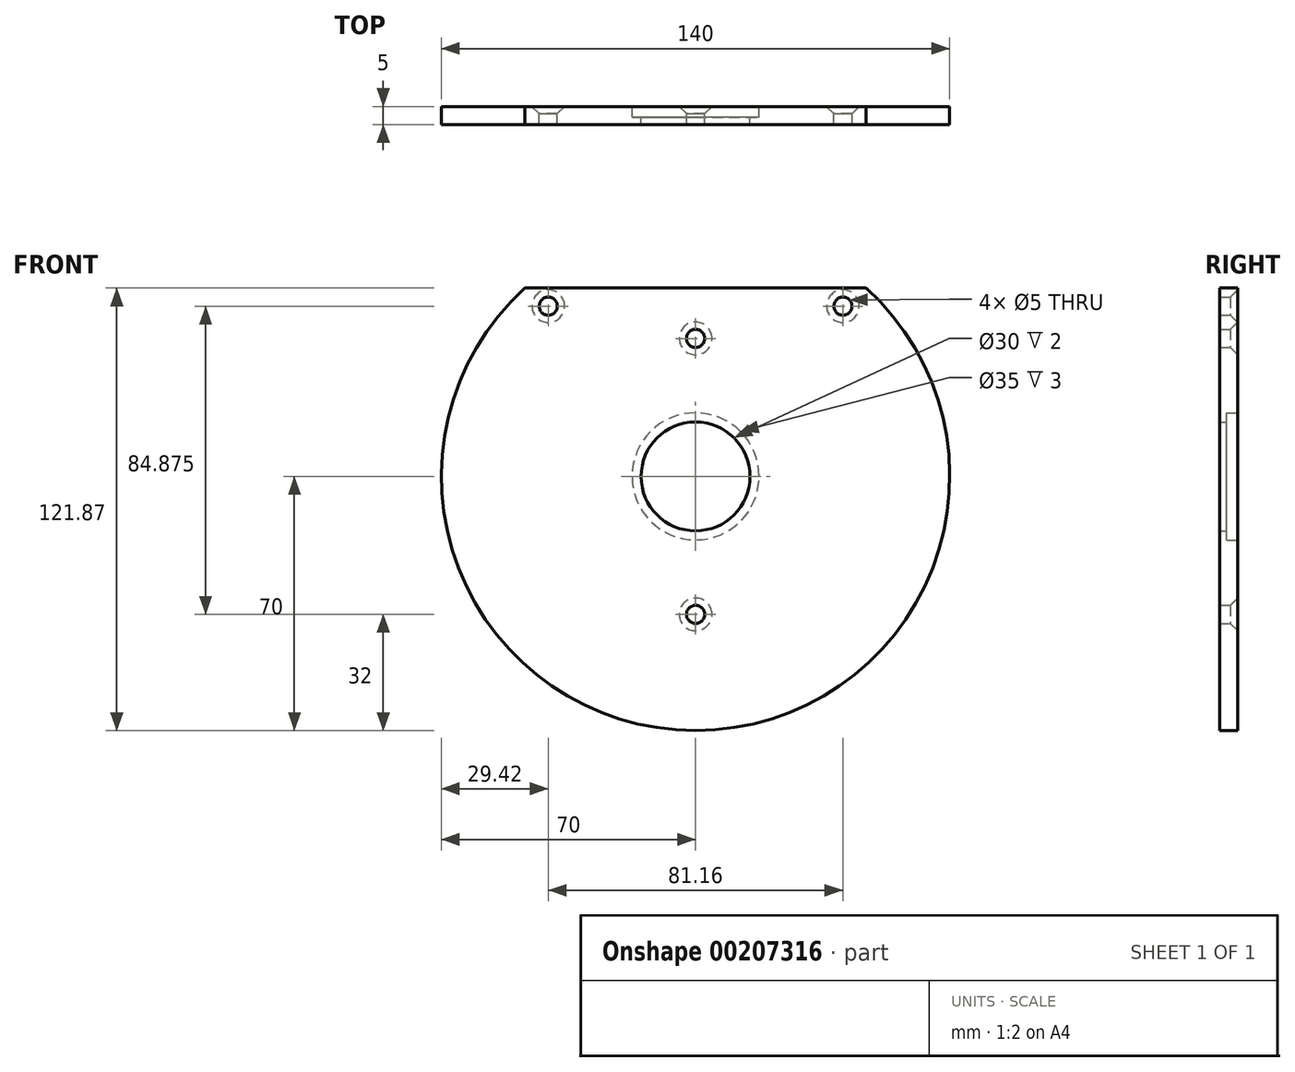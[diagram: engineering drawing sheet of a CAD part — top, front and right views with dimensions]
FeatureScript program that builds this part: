
annotation { "Feature Type Name" : "Feature", "Feature Type Description" : "" }
export const myFeature = defineFeature(function(context is Context, id is Id, definition is map)
    precondition{}
    {
        {
            assignVariable(context, id + "F0", {"name" : "T", "anyValue" : 5});
        }
        {
            assignVariable(context, id + "F1", {"name" : "dia", "anyValue" : 5});
        }
        {
            var Q0;
            Q0=qCreatedBy(makeId("Front.planeOp"),FACE);
            var sketch = newSketch(context, id + "F2", { "sketchPlane" : qUnion([Q0])});
            skArc(sketch, "E0", {"start": v(-47, 51.87) * mm, "mid": v(0, -70) * mm, "end": v(47, 51.87) * mm});
            skCircle(sketch, "E1", {"center": v(0, 0) * mm, "radius": 15 * mm});
            skLineSegment(sketch, "E2", {"start": v(-47, 51.87) * mm, "end": v(47, 51.87) * mm});
            skLineSegment(sketch, "E3", {"start": v(-51.99, 46.87) * mm, "end": v(51.99, 46.87) * mm, "construction": true});
            skCircle(sketch, "E4", {"center": v(0, 0) * mm, "radius": 62 * mm, "construction": true});
            skCircle(sketch, "E5", {"center": v(-40.58, 46.87) * mm, "radius": 2.5 * mm});
            skCircle(sketch, "E6", {"center": v(40.58, 46.87) * mm, "radius": 2.5 * mm});
            skCircle(sketch, "E7", {"center": v(0, 0) * mm, "radius": 38 * mm, "construction": true});
            skCircle(sketch, "E8", {"center": v(0, 38) * mm, "radius": 2.5 * mm});
            skCircle(sketch, "E9", {"center": v(0, -38) * mm, "radius": 2.5 * mm});
            skCircle(sketch, "E10", {"center": v(0, 0) * mm, "radius": 17.5 * mm});
            skSolve(sketch);
        }
        {
            var Q0;
            Q0=makeQuery(id+"F2.imprint","IMPRINT",FACE,{"disambiguationData":[TD([[makeQuery(id+"F2.imprint","IMPRINT",EDGE,{"derivedFrom":sQuery(id+"F2.wireOp",EDGE,"E0")}),1.0]])]});
            var Q1;
            Q1=makeQuery(id+"F2.imprint","IMPRINT",FACE,{"disambiguationData":[TD([[makeQuery(id+"F2.imprint","IMPRINT",EDGE,{"derivedFrom":sQuery(id+"F2.wireOp",EDGE,"E6")}),1.0]])]});
            var Q2;
            Q2=makeQuery(id+"F2.imprint","IMPRINT",FACE,{"disambiguationData":[TD([[makeQuery(id+"F2.imprint","IMPRINT",EDGE,{"derivedFrom":sQuery(id+"F2.wireOp",EDGE,"E8")}),1.0]])]});
            var Q3;
            Q3=makeQuery(id+"F2.imprint","IMPRINT",FACE,{"disambiguationData":[TD([[makeQuery(id+"F2.imprint","IMPRINT",EDGE,{"derivedFrom":sQuery(id+"F2.wireOp",EDGE,"E5")}),1.0]])]});
            var Q4;
            Q4=makeQuery(id+"F2.imprint","IMPRINT",FACE,{"disambiguationData":[TD([[makeQuery(id+"F2.imprint","IMPRINT",EDGE,{"derivedFrom":sQuery(id+"F2.wireOp",EDGE,"E9")}),1.0]])]});
            var Q5;
            Q5=makeQuery(id+"F2.imprint","IMPRINT",FACE,{"disambiguationData":[TD([[makeQuery(id+"F2.imprint","IMPRINT",EDGE,{"derivedFrom":sQuery(id+"F2.wireOp",EDGE,"E1")}),-1.0]])]});
            extrude(context, id + "F3", {"entities" : qUnion([Q0, Q1, Q2, Q3, Q4, Q5]), "depth" : getVariable(context, 'T') * mm});
        }
        {
            var Q0;
            Q0=makeQuery(id+"F2.imprint","IMPRINT",FACE,{"disambiguationData":[TD([[makeQuery(id+"F2.imprint","IMPRINT",EDGE,{"derivedFrom":sQuery(id+"F2.wireOp",EDGE,"E1")}),-1.0]])]});
            extrude(context, id + "F4", {"entities" : qUnion([Q0]), "operationType" : NewBodyOperationType.REMOVE, "depth" : 3 * mm});
        }
        {
            var Q0;
            Q0=sQuery(id+"F2.wireOp",VERTEX,"E5.center");
            var Q1;
            Q1=sQuery(id+"F2.wireOp",VERTEX,"E8.center");
            var Q2;
            Q2=sQuery(id+"F2.wireOp",VERTEX,"E6.center");
            var Q3;
            Q3=sQuery(id+"F2.wireOp",VERTEX,"E9.center");
            var Q4;
            Q4=makeQuery(id+"F3.opExtrude","SWEPT_BODY",BODY,{"disambiguationData":[OSD([sQuery(id+"F2.wireOp",EDGE,"E0"),sQuery(id+"F2.wireOp",EDGE,"E2"),sQuery(id+"F2.wireOp",EDGE,"E10")])]});
            hole(context, id + "F5", {"style" : HoleStyle.C_SINK, "endStyle" : HoleEndStyle.THROUGH, "oppositeDirection" : true, "holeDiameter" : getVariable(context, 'dia') * mm, "cSinkDiameter" : 9 * mm, "cSinkAngle" : 90 * degree, "locations" : qUnion([Q0, Q1, Q2, Q3]), "scope" : qUnion([Q4]), "isTappedThrough" : true});
        }
    });
